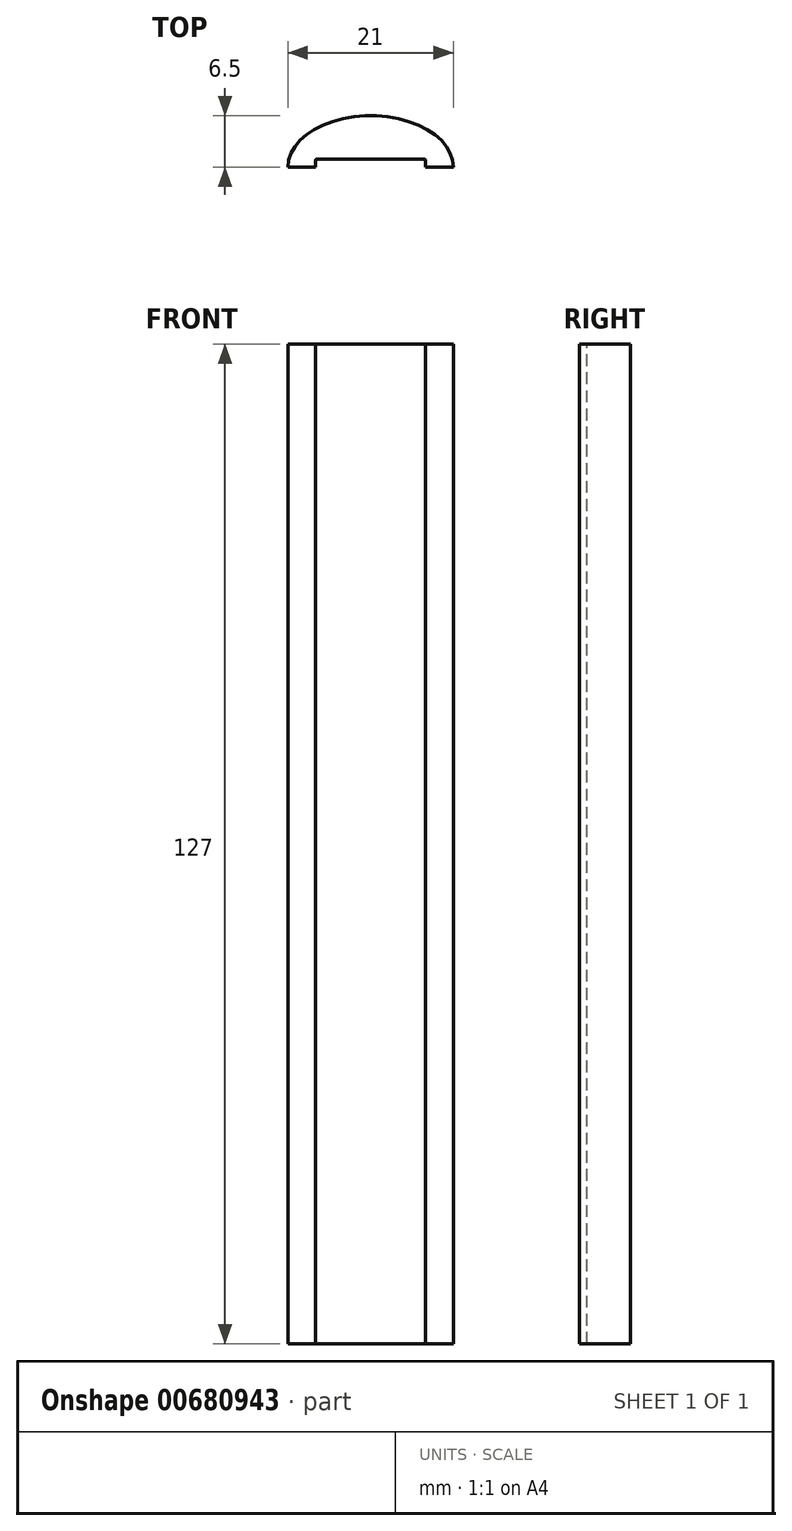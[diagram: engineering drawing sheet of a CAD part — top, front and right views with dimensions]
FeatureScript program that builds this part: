
annotation { "Feature Type Name" : "Feature", "Feature Type Description" : "" }
export const myFeature = defineFeature(function(context is Context, id is Id, definition is map)
    precondition{}
    {
        {
            var Q0;
            Q0=qCreatedBy(makeId("Top.planeOp"),FACE);
            var sketch = newSketch(context, id + "F0", { "sketchPlane" : qUnion([Q0])});
            skEllipticalArc(sketch, "E0", {});
            skLineSegment(sketch, "E1", {"start": v(-10.5, 0) * mm, "end": v(10.5, 0) * mm});
            const initialGuessF0  = {"E0": [0, 0, -1, 0, 0.0105, 0.0065, 3.141592653589793, 0]};
            skSetInitialGuess(sketch, initialGuessF0);
            skSolve(sketch);
        }
        {
            var Q0;
            Q0=qCreatedBy(makeId("Right.planeOp"),FACE);
            var sketch = newSketch(context, id + "F1", { "sketchPlane" : qUnion([Q0])});
            skLineSegment(sketch, "E2", {"start": v(0, 0) * mm, "end": v(0, -127) * mm});
            skSolve(sketch);
        }
        {
            var Q0;
            Q0=makeQuery(id+"F0.imprint","IMPRINT",FACE,{"disambiguationData":[TD([[makeQuery(id+"F0.imprint","IMPRINT",EDGE,{"derivedFrom":sQuery(id+"F0.wireOp",EDGE,"E0")}),1.0]])]});
            var Q1;
            Q1=sQuery(id+"F1.wireOp",EDGE,"E2");
            sweep(context, id + "F2", {"profiles" : qUnion([Q0]), "path" : qUnion([Q1])});
        }
        {
            var Q0;
            Q0=makeQuery(id+"F2.opSweep","CAP_FACE",FACE,{"disambiguationData":[OSD([sQuery(id+"F0.wireOp",EDGE,"E0"),sQuery(id+"F0.wireOp",EDGE,"E1"),sQuery(id+"F1.wireOp",VERTEX,"E2.start")])],"isStart":true});
            var sketch = newSketch(context, id + "F3", { "sketchPlane" : qUnion([Q0])});
            skLineSegment(sketch, "E3", {"start": v(0, 0) * mm, "end": v(-7, 0) * mm});
            skLineSegment(sketch, "E4", {"start": v(0, 0) * mm, "end": v(7, 0) * mm});
            skLineSegment(sketch, "E5", {"start": v(-7, 0) * mm, "end": v(-7, 0.8) * mm});
            skLineSegment(sketch, "E6", {"start": v(-6.8, 1) * mm, "end": v(6.8, 1) * mm});
            skLineSegment(sketch, "E7", {"start": v(7, 0.8) * mm, "end": v(7, 0) * mm});
            skPoint(sketch, "E8.visualSharp", {"position": v(-7, 1) * mm});
            skArc(sketch, "E8.filletArc", {"start": v(-6.8, 1) * mm, "mid": v(-6.94, 0.94) * mm, "end": v(-7, 0.8) * mm});
            skPoint(sketch, "E9.visualSharp", {"position": v(7, 1) * mm});
            skArc(sketch, "E9.filletArc", {"start": v(7, 0.8) * mm, "mid": v(6.94, 0.94) * mm, "end": v(6.8, 1) * mm});
            skSolve(sketch);
        }
        {
            var Q0;
            Q0=makeQuery(id+"F3.imprint","IMPRINT",FACE,{"disambiguationData":[TD([[makeQuery(id+"F3.imprint","IMPRINT",EDGE,{"derivedFrom":sQuery(id+"F3.wireOp",EDGE,"E3")}),-1.0]])]});
            extrude(context, id + "F4", {"entities" : qUnion([Q0]), "operationType" : NewBodyOperationType.REMOVE, "oppositeDirection" : true, "depth" : 127 * mm, "offsetDistance" : 25 * mm});
        }
    });
